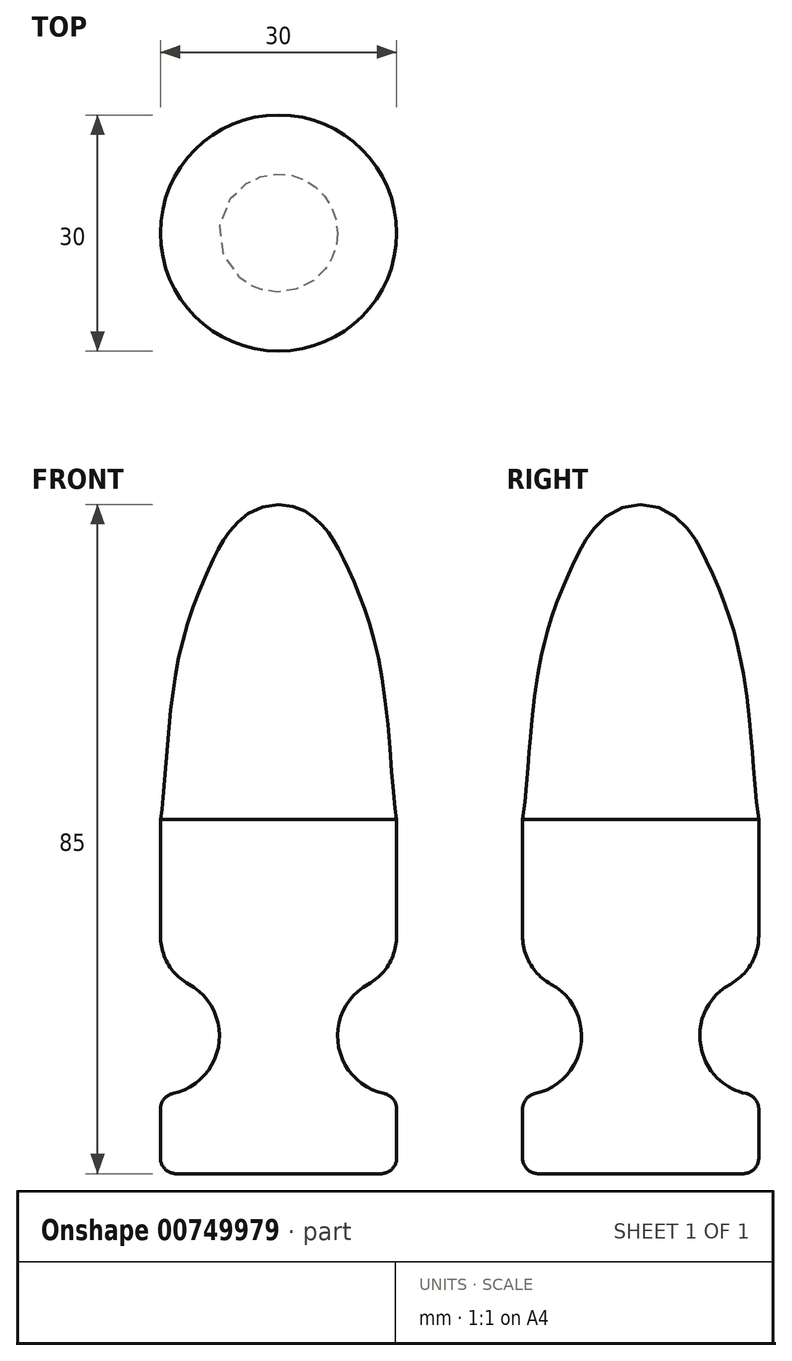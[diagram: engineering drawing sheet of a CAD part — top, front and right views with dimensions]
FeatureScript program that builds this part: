
annotation { "Feature Type Name" : "Feature", "Feature Type Description" : "" }
export const myFeature = defineFeature(function(context is Context, id is Id, definition is map)
    precondition{}
    {
        {
            var Q0;
            Q0=qCreatedBy(makeId("Front.planeOp"),FACE);
            var sketch = newSketch(context, id + "F0", { "sketchPlane" : qUnion([Q0])});
            skLineSegment(sketch, "E0", {"start": v(0, 0) * mm, "end": v(15, 0) * mm, "construction": true});
            skLineSegment(sketch, "E1", {"start": v(15, 0) * mm, "end": v(15, 60) * mm, "construction": true});
            skLineSegment(sketch, "E2", {"start": v(0, 69.29) * mm, "end": v(0, -50.49) * mm, "construction": true});
            skLineSegment(sketch, "E3", {"start": v(15, 60) * mm, "end": v(0, 60) * mm, "construction": true});
            skPoint(sketch, "E4", {"position": v(15, 20) * mm});
            skFitSpline(sketch, "E5", {"points": [v(15, 20) * mm, v(13.39, 36.4) * mm, v(10.2, 48.71) * mm, v(7.59, 54.4) * mm, v(5.45, 57.48) * mm, v(0, 60) * mm], "startDerivative": vector(-5.28, 22.14) * mm, "endDerivative": vector(-45.91, 0) * mm});
            skLineSegment(sketch, "E6", {"start": v(15, 20) * mm, "end": v(15, 0) * mm});
            skLineSegment(sketch, "E7", {"start": v(15, 0) * mm, "end": v(15, -15) * mm, "construction": true});
            skLineSegment(sketch, "E8.top", {"start": v(15, -25) * mm, "end": v(0, -25) * mm});
            skLineSegment(sketch, "E8.left", {"start": v(15, -15) * mm, "end": v(15, -25) * mm});
            skLineSegment(sketch, "E8.right", {"start": v(0, -15) * mm, "end": v(0, -25) * mm, "construction": true});
            skArc(sketch, "E9", {"start": v(15, 0) * mm, "mid": v(7.5, -7.5) * mm, "end": v(15, -15) * mm});
            skLineSegment(sketch, "E10", {"start": v(0, 60) * mm, "end": v(0, -25) * mm});
            skSolve(sketch);
        }
        {
            var Q0;
            Q0=makeQuery(id+"F0.imprint","IMPRINT",FACE,{"disambiguationData":[TD([[makeQuery(id+"F0.imprint","IMPRINT",EDGE,{"derivedFrom":sQuery(id+"F0.wireOp",EDGE,"E5")}),1.0]])]});
            var Q1;
            Q1=sQuery(id+"F0.wireOp",EDGE,"E2");
            revolve(context, id + "F1", {"surfaceOperationType" : NewSurfaceOperationType.NEW, "entities" : qUnion([Q0]), "axis" : qUnion([Q1]), "revolveType" : RevolveType.FULL});
        }
        {
            var Q0;
            Q0=makeQuery(id+"F1.opRevolve","SWEPT_EDGE",EDGE,{"disambiguationData":[OSD([sQuery(id+"F0.wireOp",EDGE,"E8.left"),sQuery(id+"F0.wireOp",EDGE,"E9")])]});
            var Q1;
            Q1=makeQuery(id+"F1.opRevolve","SWEPT_EDGE",EDGE,{"disambiguationData":[OSD([sQuery(id+"F0.wireOp",EDGE,"E8.top"),sQuery(id+"F0.wireOp",EDGE,"E8.left")])]});
            fillet(context, id + "F2", {"entities" : qUnion([Q0, Q1]), "radius" : 2 * mm, "tangentPropagation" : true, "defaultsChanged" : false, "vertexSettings" : [], "allowEdgeOverflow" : false});
        }
        {
            var Q0;
            Q0=makeQuery(id+"F1.opRevolve","SWEPT_EDGE",EDGE,{"disambiguationData":[OSD([sQuery(id+"F0.wireOp",EDGE,"E6"),sQuery(id+"F0.wireOp",EDGE,"E9")])]});
            fillet(context, id + "F3", {"entities" : qUnion([Q0]), "radius" : 7 * mm, "tangentPropagation" : true, "allowEdgeOverflow" : false});
        }
    });
